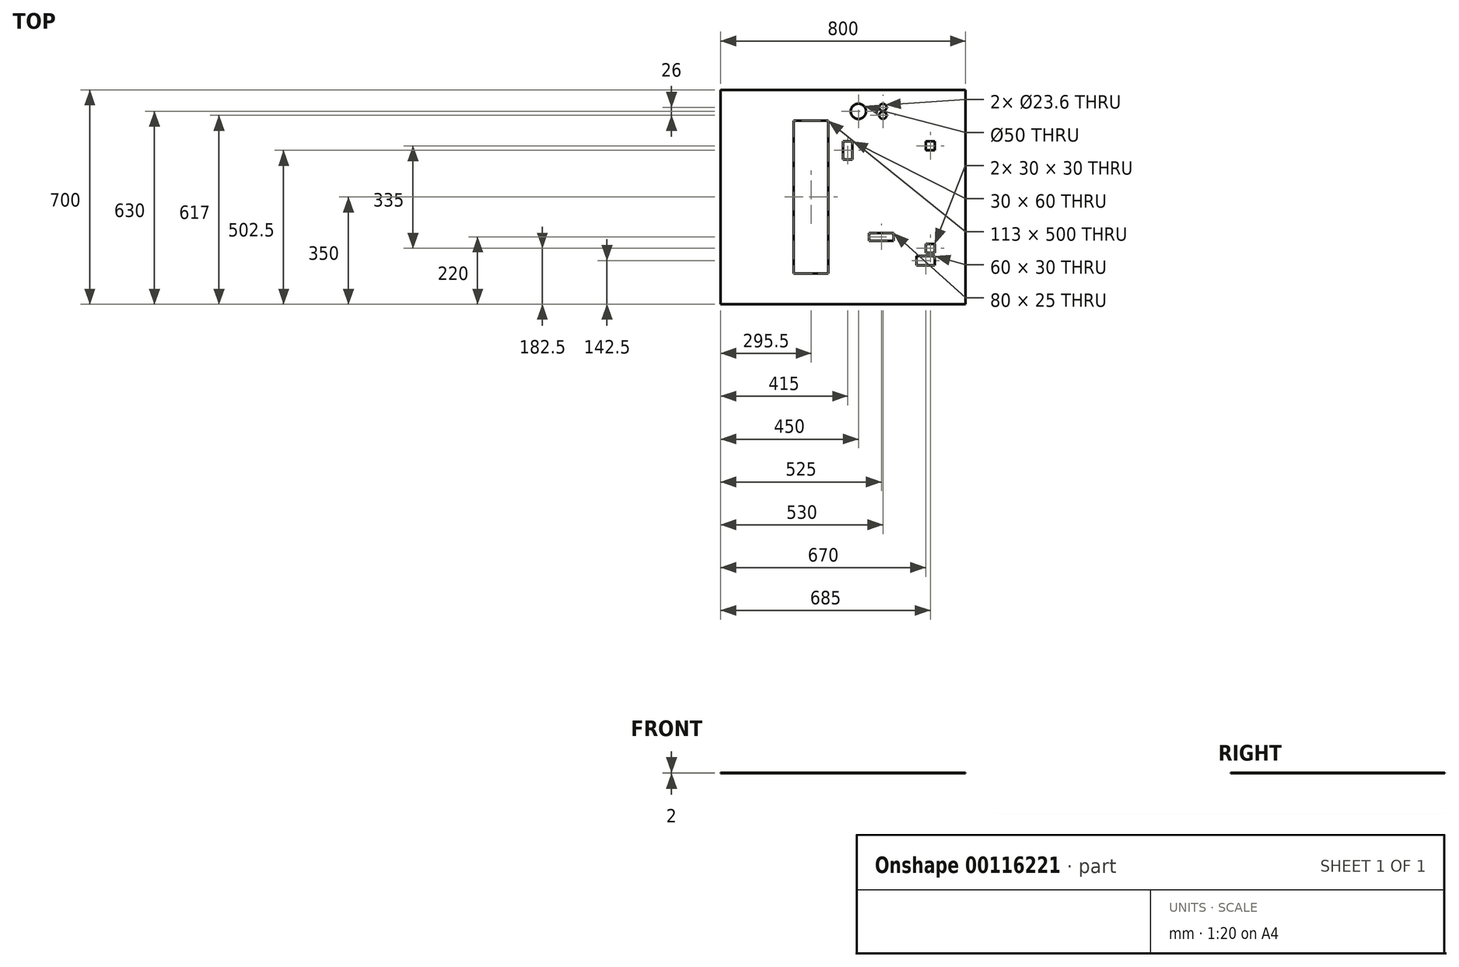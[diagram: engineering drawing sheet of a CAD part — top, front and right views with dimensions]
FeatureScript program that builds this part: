
annotation { "Feature Type Name" : "Feature", "Feature Type Description" : "" }
export const myFeature = defineFeature(function(context is Context, id is Id, definition is map)
    precondition{}
    {
        {
            var Q0;
            Q0=qCreatedBy(makeId("Top.planeOp"),FACE);
            var sketch = newSketch(context, id + "F0", { "sketchPlane" : qUnion([Q0])});
            skLineSegment(sketch, "E0.bottom", {"start": v(0, 0) * mm, "end": v(800, 0) * mm});
            skLineSegment(sketch, "E0.top", {"start": v(0, 700) * mm, "end": v(800, 700) * mm});
            skLineSegment(sketch, "E0.left", {"start": v(0, 0) * mm, "end": v(0, 700) * mm});
            skLineSegment(sketch, "E0.right", {"start": v(800, 0) * mm, "end": v(800, 700) * mm});
            skLineSegment(sketch, "E1.bottom", {"start": v(670, 532.5) * mm, "end": v(700, 532.5) * mm});
            skLineSegment(sketch, "E1.top", {"start": v(670, 502.5) * mm, "end": v(700, 502.5) * mm});
            skLineSegment(sketch, "E1.left", {"start": v(670, 532.5) * mm, "end": v(670, 502.5) * mm});
            skLineSegment(sketch, "E1.right", {"start": v(700, 532.5) * mm, "end": v(700, 502.5) * mm});
            skLineSegment(sketch, "E2.bottom", {"start": v(670, 197.5) * mm, "end": v(700, 197.5) * mm});
            skLineSegment(sketch, "E2.top", {"start": v(670, 167.5) * mm, "end": v(700, 167.5) * mm});
            skLineSegment(sketch, "E2.left", {"start": v(670, 197.5) * mm, "end": v(670, 167.5) * mm});
            skLineSegment(sketch, "E2.right", {"start": v(700, 197.5) * mm, "end": v(700, 167.5) * mm});
            skLineSegment(sketch, "E3.bottom", {"start": v(400, 532.5) * mm, "end": v(430, 532.5) * mm});
            skLineSegment(sketch, "E3.top", {"start": v(400, 472.5) * mm, "end": v(430, 472.5) * mm});
            skLineSegment(sketch, "E3.left", {"start": v(400, 532.5) * mm, "end": v(400, 472.5) * mm});
            skLineSegment(sketch, "E3.right", {"start": v(430, 532.5) * mm, "end": v(430, 472.5) * mm});
            skLineSegment(sketch, "E4.bottom", {"start": v(239, 600) * mm, "end": v(352, 600) * mm});
            skLineSegment(sketch, "E4.top", {"start": v(239, 100) * mm, "end": v(352, 100) * mm});
            skLineSegment(sketch, "E4.left", {"start": v(239, 600) * mm, "end": v(239, 100) * mm});
            skLineSegment(sketch, "E4.right", {"start": v(352, 600) * mm, "end": v(352, 100) * mm});
            skLineSegment(sketch, "E5", {"start": v(400, 167.5) * mm, "end": v(400, 532.5) * mm, "construction": true});
            skLineSegment(sketch, "E6", {"start": v(400, 532.5) * mm, "end": v(700, 532.5) * mm, "construction": true});
            skLineSegment(sketch, "E7", {"start": v(400, 167.5) * mm, "end": v(700, 167.5) * mm, "construction": true});
            skCircle(sketch, "E8", {"center": v(450, 630) * mm, "radius": 25 * mm});
            skLineSegment(sketch, "E9.bottom", {"start": v(640, 157.5) * mm, "end": v(700, 157.5) * mm});
            skLineSegment(sketch, "E9.top", {"start": v(640, 127.5) * mm, "end": v(700, 127.5) * mm});
            skLineSegment(sketch, "E9.left", {"start": v(640, 157.5) * mm, "end": v(640, 127.5) * mm});
            skLineSegment(sketch, "E9.right", {"start": v(700, 157.5) * mm, "end": v(700, 127.5) * mm});
            skLineSegment(sketch, "E10.bottom", {"start": v(485, 232.5) * mm, "end": v(565, 232.5) * mm});
            skLineSegment(sketch, "E10.top", {"start": v(485, 207.5) * mm, "end": v(565, 207.5) * mm});
            skLineSegment(sketch, "E10.left", {"start": v(485, 232.5) * mm, "end": v(485, 207.5) * mm});
            skLineSegment(sketch, "E10.right", {"start": v(565, 232.5) * mm, "end": v(565, 207.5) * mm});
            skCircle(sketch, "E11", {"center": v(530, 643) * mm, "radius": 11.8 * mm});
            skCircle(sketch, "E12", {"center": v(530, 617) * mm, "radius": 11.8 * mm});
            skSolve(sketch);
        }
        {
            var Q0;
            Q0 = qSketchRegion(id + "F0", true);
            extrude(context, id + "F1", {"entities" : qUnion([Q0]), "depth" : 2 * mm});
        }
    });
